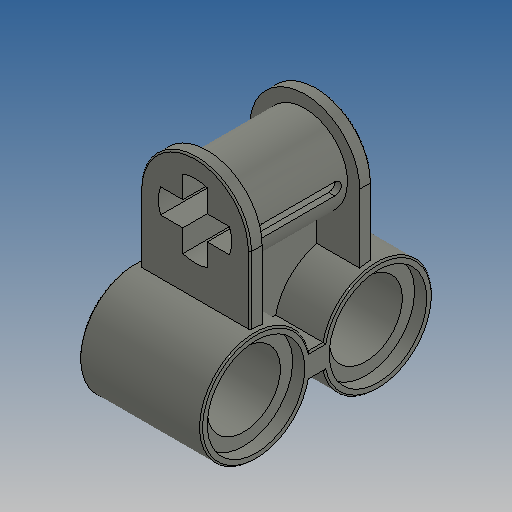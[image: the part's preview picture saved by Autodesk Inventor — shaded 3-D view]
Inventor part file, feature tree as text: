
AUTODESK INVENTOR PART (.ipt)
format: ipt  version: 2025 (Build 290162010, 162A)  size: 326,656 bytes
history: native  units: in
note: dims shown in document units (in); Inventor stores cm internally (conversion verified against a paired STEP export)
features: sketch x5, extrude x4, plane x1, revolve x1, mirror x1, fillet x1, other x1
ambient origin geometry x8: Origin, YZ Plane, XZ Plane, XY Plane, X Axis, Y Axis, Z Axis, Center Point
bodies: Solid1 (feature_tree)
feature tree (14):
  extrude  "Extrusion1"  Depth=0.063in
  plane  "Work Plane2"
  extrude  "Extrusion2"  Depth=0.315in TaperAngle=0.0deg
  extrude  "Extrusion3"  Depth=0.189in
  extrude  "Extrusion4"  Depth=0.0315in
  revolve  "Revolution1"  [1 undecoded]
  mirror  "Mirror1"
  fillet  "Fillet1"  Radius=0.063in
  sketch  "Sketch2"  dims[d0=0.2835in d1=0.063in]
  other  "Work Axis3"
  sketch  "Sketch3"  dims[d2=0.315in d3=0.315in d4=0.0in]
  sketch  "Sketch4"  dims[d6=90.0deg d7=0.189in]
  sketch  "Sketch5"  dims[d8=0.252in d9=0.0315in]
  sketch  "Sketch6"  dims[d10=90.0deg d12=0.2205in d14=0.063in d18=0.189in d20=0.063in d21=0.315in d22=0.0in d23=0.0315in d24=0.2205in d25=0.315in d26=0.0in d29=0.0315in d30=0.0in d39=0.0039in d40=0.315in d41=0.2835in d42=0.252in]
note: 1 required parameter value undecoded (feature->parameter linkage not recoverable at this tier; creation-order binding heuristic only, values carry confidence <= 0.55)
